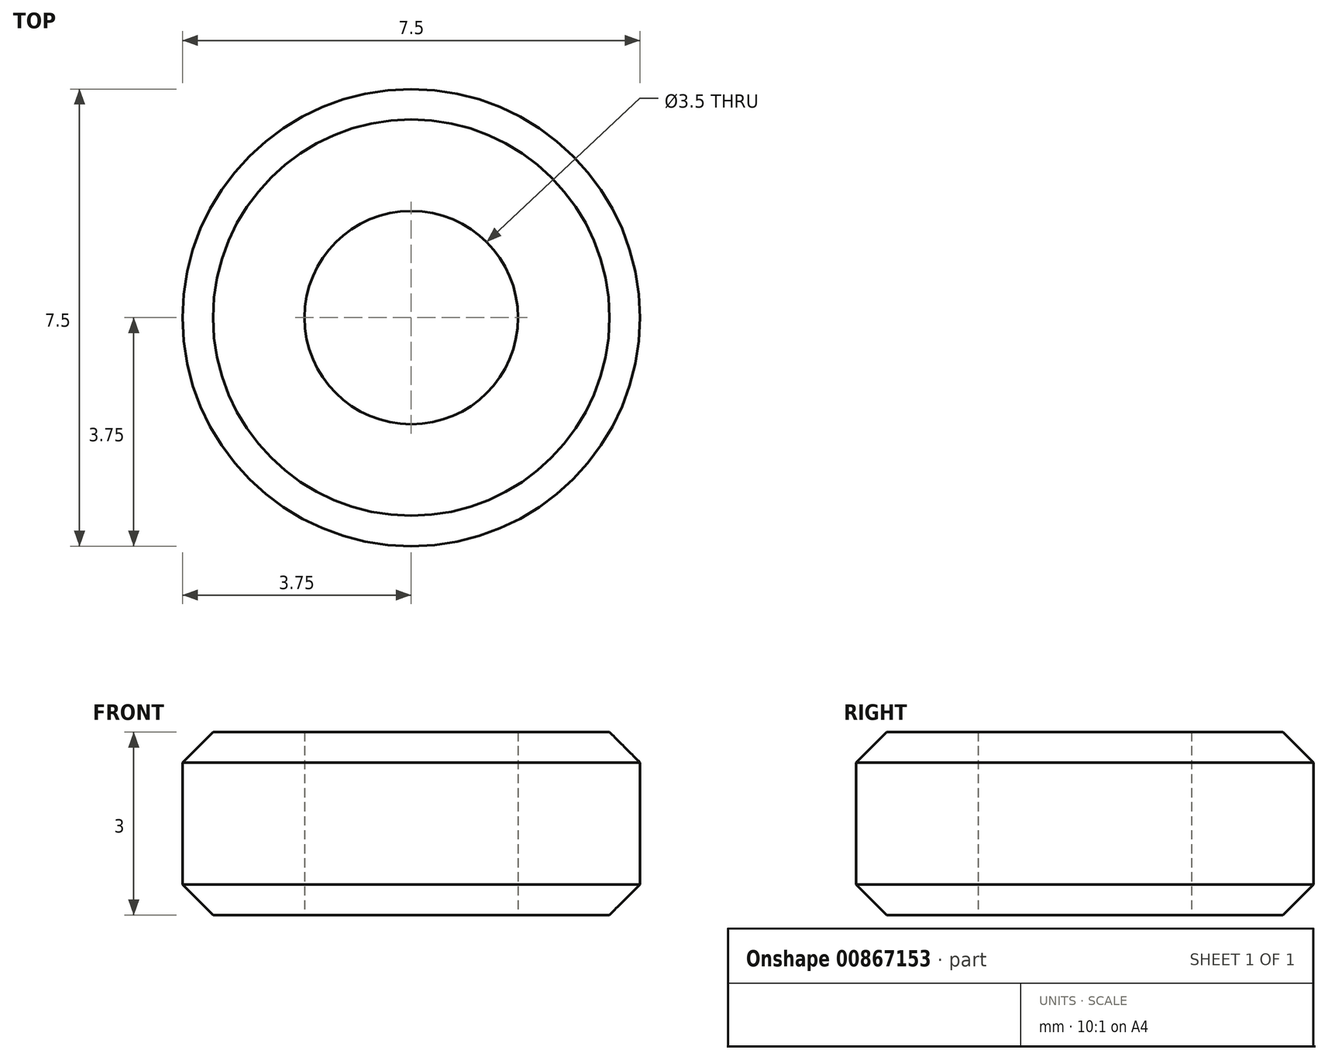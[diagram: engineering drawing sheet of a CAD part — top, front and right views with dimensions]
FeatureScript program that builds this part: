
annotation { "Feature Type Name" : "Feature", "Feature Type Description" : "" }
export const myFeature = defineFeature(function(context is Context, id is Id, definition is map)
    precondition{}
    {
        {
            var Q0;
            Q0=qCreatedBy(makeId("Top.planeOp"),FACE);
            var sketch = newSketch(context, id + "F0", { "sketchPlane" : qUnion([Q0])});
            skCircle(sketch, "E0", {"center": v(0, 0) * mm, "radius": 1.75 * mm});
            skCircle(sketch, "E1", {"center": v(0, 0) * mm, "radius": 3.75 * mm});
            skSolve(sketch);
        }
        {
            var Q0;
            Q0=makeQuery(id+"F0.imprint","IMPRINT",FACE,{"disambiguationData":[TD([[makeQuery(id+"F0.imprint","IMPRINT",EDGE,{"derivedFrom":sQuery(id+"F0.wireOp",EDGE,"E0")}),-1.0]])]});
            extrude(context, id + "F1", {"entities" : qUnion([Q0]), "depth" : 3 * mm, "offsetDistance" : 25 * mm});
        }
        {
            var Q0;
            Q0=makeQuery(id+"F1.opExtrude","CAP_EDGE",EDGE,{"disambiguationData":[OSD([sQuery(id+"F0.wireOp",EDGE,"E1")])],"isStart":false});
            var Q1;
            Q1=makeQuery(id+"F1.opExtrude","CAP_EDGE",EDGE,{"disambiguationData":[OSD([sQuery(id+"F0.wireOp",EDGE,"E1")])],"isStart":true});
            chamfer(context, id + "F2", {"entities" : qUnion([Q0, Q1]), "width" : .5 * mm, "tangentPropagation" : true});
        }
    });
